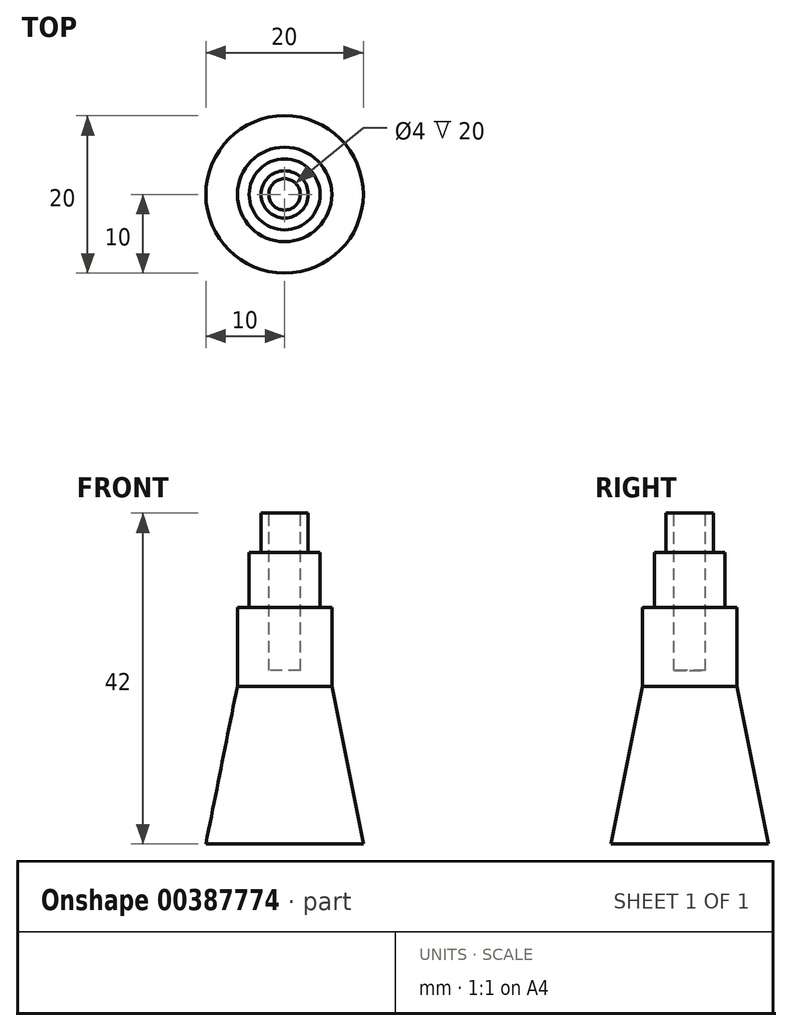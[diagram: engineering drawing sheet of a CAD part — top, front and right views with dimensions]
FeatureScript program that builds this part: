
annotation { "Feature Type Name" : "Feature", "Feature Type Description" : "" }
export const myFeature = defineFeature(function(context is Context, id is Id, definition is map)
    precondition{}
    {
        {
            var Q0;
            Q0=qCreatedBy(makeId("Top.planeOp"),FACE);
            var sketch = newSketch(context, id + "F0", { "sketchPlane" : qUnion([Q0])});
            skCircle(sketch, "E0", {"center": v(0, 0) * mm, "radius": 4.5 * mm});
            skSolve(sketch);
        }
        {
            var Q0;
            Q0 = qSketchRegion(id + "F0", true);
            extrude(context, id + "F1", {"entities" : qUnion([Q0]), "depth" : 7 * mm});
        }
        {
            var Q0;
            Q0=makeQuery(id+"F1.opExtrude","CAP_FACE",FACE,{"disambiguationData":[OSD([sQuery(id+"F0.wireOp",EDGE,"E0")])],"isStart":false});
            var sketch = newSketch(context, id + "F2", { "sketchPlane" : qUnion([Q0])});
            skCircle(sketch, "E1", {"center": v(0, 0) * mm, "radius": 3 * mm});
            skSolve(sketch);
        }
        {
            var Q0;
            Q0 = qSketchRegion(id + "F2", true);
            var Q1;
            Q1 = qSketchRegion(id + "F0", true);
            extrude(context, id + "F3", {"entities" : qUnion([Q0, Q1]), "operationType" : NewBodyOperationType.ADD, "depth" : 5 * mm});
        }
        {
            var Q0;
            Q0=makeQuery(id+"F1.opExtrude","CAP_FACE",FACE,{"disambiguationData":[OSD([sQuery(id+"F0.wireOp",EDGE,"E0")])],"isStart":true});
            var sketch = newSketch(context, id + "F4", { "sketchPlane" : qUnion([Q0])});
            skCircle(sketch, "E2", {"center": v(0, 0) * mm, "radius": 6 * mm});
            skSolve(sketch);
        }
        {
            var Q0;
            Q0 = qSketchRegion(id + "F4", true);
            extrude(context, id + "F5", {"entities" : qUnion([Q0]), "operationType" : NewBodyOperationType.ADD, "depth" : 10 * mm});
        }
        {
            var Q0;
            Q0=makeQuery(id+"F5.opExtrude","CAP_FACE",FACE,{"disambiguationData":[OSD([sQuery(id+"F4.wireOp",EDGE,"E2")])],"isStart":false});
            var sketch = newSketch(context, id + "F6", { "sketchPlane" : qUnion([Q0])});
            skSolve(sketch);
        }
        {
            var Q0;
            Q0=qCreatedBy(makeId("Top.planeOp"),FACE);
            var Q1;
            Q1 = qBodyType(qCreatedBy(id + "F8" ,EDGE), BodyType.WIRE);
            cPlane(context, id + "F7", {"entities" : qUnion([Q0, Q1]), "cplaneType" : CPlaneType.OFFSET, "offset" : 30 * mm, "oppositeDirection" : true, "width" : 150 * mm, "height" : 150 * mm});
        }
        {
            var Q0;
            Q0=qCreatedBy(id+"F7.planeOp",FACE);
            var sketch = newSketch(context, id + "F8", { "sketchPlane" : qUnion([Q0])});
            skCircle(sketch, "E3", {"center": v(0, 0) * mm, "radius": 10 * mm});
            skSolve(sketch);
        }
        {
            var Q0;
            Q0=makeQuery(id+"F8.imprint","IMPRINT",FACE,{"disambiguationData":[TD([[makeQuery(id+"F8.imprint","IMPRINT",EDGE,{"derivedFrom":sQuery(id+"F8.wireOp",EDGE,"E3")}),1.0]])]});
            var Q1;
            Q1=makeQuery(id+"F6.imprint","IMPRINT",FACE,{"disambiguationData":[TD([[makeQuery(id+"F6.imprint","IMPRINT",EDGE,{"derivedFrom":makeQuery(id+"F5.opExtrude","CAP_EDGE",EDGE,{"disambiguationData":[OSD([sQuery(id+"F4.wireOp",EDGE,"E2")])],"isStart":false})}),1.0]])]});
            loft(context, id + "F9", {"sheetProfilesArray" : [{ "sheetProfileEntities" : qUnion([Q0]) }, { "sheetProfileEntities" : qUnion([Q1]) }]});
        }
        {
            var Q0;
            Q0=makeQuery(id+"F3.opExtrude","CAP_FACE",FACE,{"disambiguationData":[OSD([sQuery(id+"F2.wireOp",EDGE,"E1")])],"isStart":false});
            var sketch = newSketch(context, id + "F10", { "sketchPlane" : qUnion([Q0])});
            skCircle(sketch, "E4", {"center": v(0, 0) * mm, "radius": 2 * mm});
            skSolve(sketch);
        }
        {
            var Q0;
            Q0 = qSketchRegion(id + "F10", true);
            extrude(context, id + "F11", {"entities" : qUnion([Q0]), "operationType" : NewBodyOperationType.REMOVE, "oppositeDirection" : true, "depth" : 20 * mm});
        }
    });
